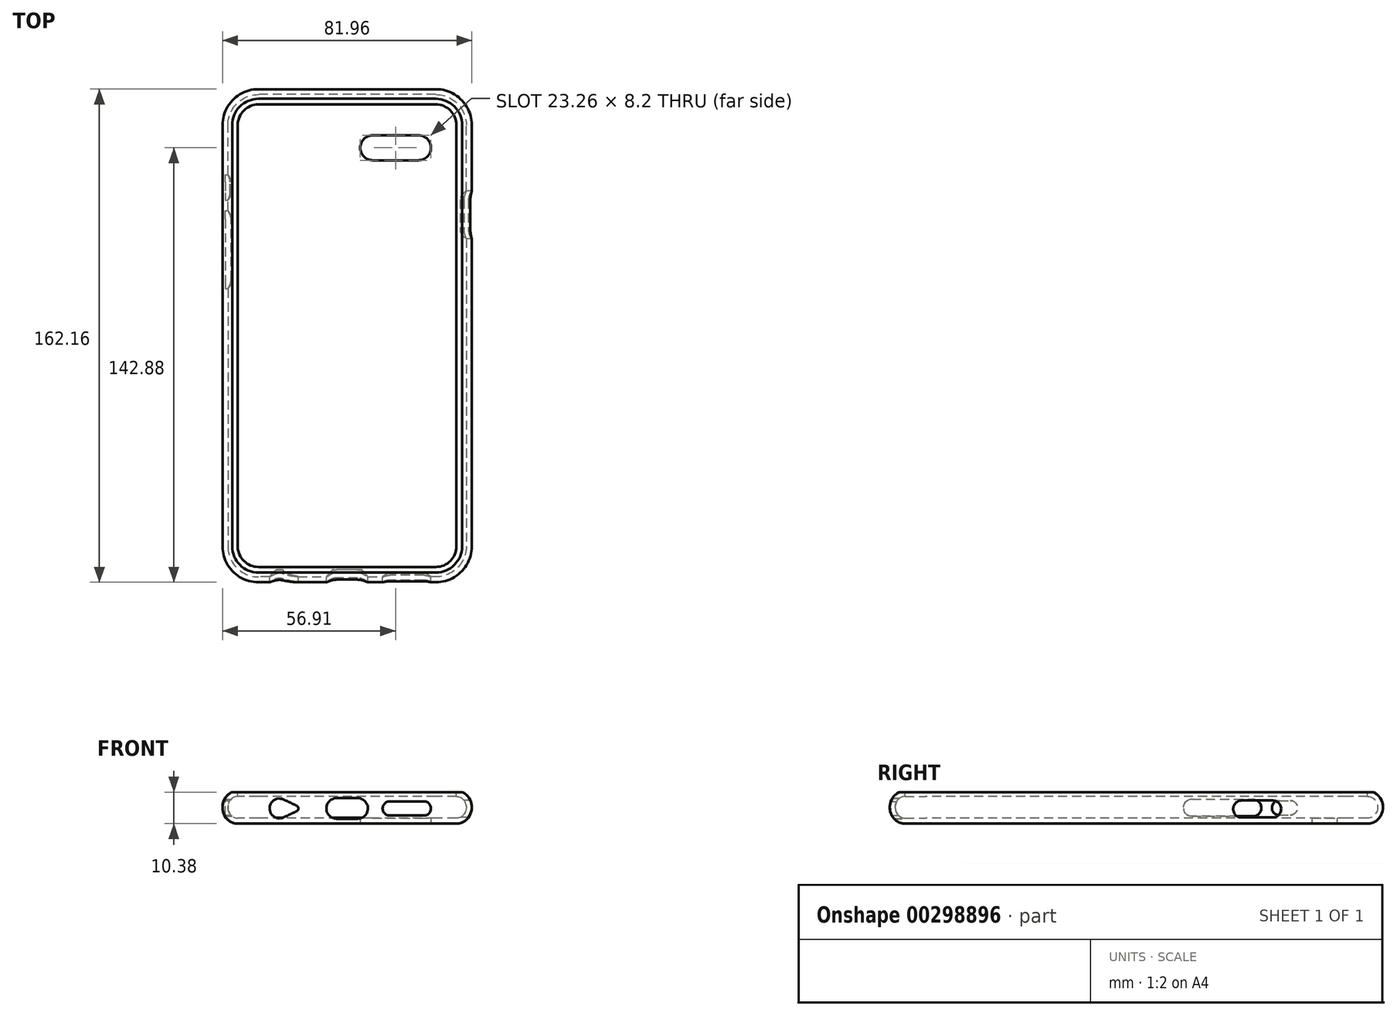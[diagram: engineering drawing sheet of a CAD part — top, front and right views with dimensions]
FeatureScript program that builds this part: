
annotation { "Feature Type Name" : "Feature", "Feature Type Description" : "" }
export const myFeature = defineFeature(function(context is Context, id is Id, definition is map)
    precondition{}
    {
        {
            var Q0;
            Q0=qCreatedBy(makeId("Top.planeOp"),FACE);
            var sketch = newSketch(context, id + "F0", { "sketchPlane" : qUnion([Q0])});
            skLineSegment(sketch, "E0.bottom", {"start": v(-41.5, 82.5) * mm, "end": v(41.5, 82.5) * mm});
            skLineSegment(sketch, "E0.top", {"start": v(-41.5, -82.5) * mm, "end": v(41.5, -82.5) * mm});
            skLineSegment(sketch, "E0.left", {"start": v(-41.5, 82.5) * mm, "end": v(-41.5, -82.5) * mm});
            skLineSegment(sketch, "E0.right", {"start": v(41.5, 82.5) * mm, "end": v(41.5, -82.5) * mm});
            skPoint(sketch, "E0.middle", {"position": v(0, 0) * mm});
            skSolve(sketch);
        }
        {
            var Q0;
            Q0=qSketchRegion(id+"F0",true);
            extrude(context, id + "F1", {"entities" : qUnion([Q0]), "depth" : 10 * mm});
        }
        {
            var Q0;
            Q0=makeQuery(id+"F1.opExtrude","CAP_FACE",FACE,{"disambiguationData":[OSD([sQuery(id+"F0.wireOp",EDGE,"E0.bottom"),sQuery(id+"F0.wireOp",EDGE,"E0.top"),sQuery(id+"F0.wireOp",EDGE,"E0.left"),sQuery(id+"F0.wireOp",EDGE,"E0.right")])],"isStart":false});
            var sketch = newSketch(context, id + "F2", { "sketchPlane" : qUnion([Q0])});
            skLineSegment(sketch, "E1.bottom", {"start": v(-29.15, 79.05) * mm, "end": v(29.15, 79.05) * mm});
            skLineSegment(sketch, "E1.top", {"start": v(-29.15, -79.05) * mm, "end": v(29.15, -79.05) * mm});
            skLineSegment(sketch, "E1.left", {"start": v(-38.95, 69.25) * mm, "end": v(-38.95, -69.25) * mm});
            skLineSegment(sketch, "E1.right", {"start": v(38.95, 69.25) * mm, "end": v(38.95, -69.25) * mm});
            skPoint(sketch, "E1.middle", {"position": v(0, 0) * mm});
            skPoint(sketch, "E2.visualSharp", {"position": v(-38.95, 79.05) * mm});
            skArc(sketch, "E2.filletArc", {"start": v(-29.15, 79.05) * mm, "mid": v(-36.08, 76.18) * mm, "end": v(-38.95, 69.25) * mm});
            skPoint(sketch, "E3.visualSharp", {"position": v(38.95, 79.05) * mm});
            skArc(sketch, "E3.filletArc", {"start": v(38.95, 69.25) * mm, "mid": v(36.08, 76.18) * mm, "end": v(29.15, 79.05) * mm});
            skPoint(sketch, "E4.visualSharp", {"position": v(38.95, -79.05) * mm});
            skArc(sketch, "E4.filletArc", {"start": v(29.15, -79.05) * mm, "mid": v(36.08, -76.18) * mm, "end": v(38.95, -69.25) * mm});
            skPoint(sketch, "E5.visualSharp", {"position": v(-38.95, -79.05) * mm});
            skArc(sketch, "E5.filletArc", {"start": v(-38.95, -69.25) * mm, "mid": v(-36.08, -76.18) * mm, "end": v(-29.15, -79.05) * mm});
            skSolve(sketch);
        }
        {
            var Q0;
            Q0=sQuery(id+"F2.wireOp",VERTEX,"E1.left.end");
            var Q1;
            Q1=sQuery(id+"F2.wireOp",EDGE,"E1.left");
            cPlane(context, id + "F3", {"entities" : qUnion([Q0, Q1]), "cplaneType" : CPlaneType.CURVE_POINT, "offset" : 25 * mm, "width" : 150 * mm, "height" : 150 * mm});
        }
        {
            var Q0;
            Q0=qCreatedBy(id+"F3.planeOp",FACE);
            var sketch = newSketch(context, id + "F4", { "sketchPlane" : qUnion([Q0])});
            skEllipse(sketch, "E6", {"center": v(-35.95, 5) * mm, "majorRadius": 3.6 * mm, "minorRadius": 3.25 * mm, "majorAxis": v(0, 1)});
            skLineSegment(sketch, "E7", {"start": v(0, 0) * mm, "end": v(0, 10) * mm});
            skPoint(sketch, "E8", {"position": v(-39.2, 5) * mm});
            skLineSegment(sketch, "E9", {"start": v(0, 5) * mm, "end": v(-39.2, 5) * mm});
            skPoint(sketch, "E10.oppositeSnap0", {"position": v(-35.95, 1.4) * mm});
            skPoint(sketch, "E11", {"position": v(-30.3, 10) * mm});
            skPoint(sketch, "E12", {"position": v(-32.78, 10) * mm});
            skPoint(sketch, "E13", {"position": v(-32.78, 1.4) * mm});
            skLineSegment(sketch, "E14.bottom", {"start": v(-35.95, 1.4) * mm, "end": v(-32.78, 1.4) * mm});
            skLineSegment(sketch, "E14.top", {"start": v(-35.95, 10) * mm, "end": v(-32.78, 10) * mm});
            skLineSegment(sketch, "E14.left", {"start": v(-35.95, 1.4) * mm, "end": v(-35.95, 10) * mm});
            skLineSegment(sketch, "E14.right", {"start": v(-32.78, 1.4) * mm, "end": v(-32.78, 10) * mm});
            skSolve(sketch);
        }
        {
            var Q0;
            Q0=qSketchRegion(id+"F4",true);
            var Q1;
            Q1=qConstructionFilter(qBodyType(qCreatedBy(id+"F2",EDGE),BodyType.WIRE),ConstructionObject.NO);
            sweep(context, id + "F5", {"operationType" : NewBodyOperationType.REMOVE, "profiles" : qUnion([Q0]), "path" : qUnion([Q1])});
        }
        {
            var Q0;
            {var subQ0=sQuery(id+"F4.wireOp",EDGE,"E14.right");var subQ1=makeQuery(id+"F4.imprint","IMPRINT",EDGE,{"disambiguationData":[TD([[makeQuery(id+"F4.imprint","INTERSECT",VERTEX,{"derivedFrom":[sQuery(id+"F4.wireOp",EDGE,"E14.top"),subQ0]}),1.0]])],"derivedFrom":subQ0});var subQ6=sQuery(id+"F2.wireOp",EDGE,"E1.bottom");Q0=makeQuery(id+"F5.boolean.opBoolean","SPLIT",FACE,{"disambiguationData":[TD([makeQuery(id+"F5.opSweep","SWEPT_FACE",FACE,{"disambiguationData":[OSD([subQ6,subQ0]),TDD([subQ6,subQ1])]})])],"derivedFrom":makeQuery(id+"F1.opExtrude","CAP_FACE",FACE,{"disambiguationData":[OSD([sQuery(id+"F0.wireOp",EDGE,"E0.bottom"),sQuery(id+"F0.wireOp",EDGE,"E0.top"),sQuery(id+"F0.wireOp",EDGE,"E0.left"),sQuery(id+"F0.wireOp",EDGE,"E0.right")])],"isStart":false})});}
            extrude(context, id + "F6", {"entities" : qUnion([Q0]), "operationType" : NewBodyOperationType.REMOVE, "oppositeDirection" : true, "depth" : 8.6 * mm});
        }
        {
            var Q0;
            Q0=makeQuery(id+"F1.opExtrude","CAP_FACE",FACE,{"disambiguationData":[OSD([sQuery(id+"F0.wireOp",EDGE,"E0.bottom"),sQuery(id+"F0.wireOp",EDGE,"E0.top"),sQuery(id+"F0.wireOp",EDGE,"E0.left"),sQuery(id+"F0.wireOp",EDGE,"E0.right")])],"isStart":true});
            var Q1;
            {var subQ1=sQuery(id+"F0.wireOp",EDGE,"E0.left");var subQ2=sQuery(id+"F0.wireOp",EDGE,"E0.bottom");var subQ3=sQuery(id+"F0.wireOp",EDGE,"E0.right");var subQ4=sQuery(id+"F0.wireOp",EDGE,"E0.top");Q1=makeQuery(id+"F5.boolean.opBoolean","SPLIT",FACE,{"disambiguationData":[TD([makeQuery(id+"F1.opExtrude","SWEPT_FACE",FACE,{"disambiguationData":[OSD([subQ2])]})])],"derivedFrom":makeQuery(id+"F1.opExtrude","CAP_FACE",FACE,{"disambiguationData":[OSD([subQ2,subQ4,subQ1,subQ3])],"isStart":false})});}
            var Q2;
            Q2=makeQuery(id+"F1.opExtrude","SWEPT_FACE",FACE,{"disambiguationData":[OSD([sQuery(id+"F0.wireOp",EDGE,"E0.top")])]});
            var Q3;
            Q3=makeQuery(id+"F1.opExtrude","SWEPT_FACE",FACE,{"disambiguationData":[OSD([sQuery(id+"F0.wireOp",EDGE,"E0.left")])]});
            var Q4;
            Q4=makeQuery(id+"F1.opExtrude","SWEPT_FACE",FACE,{"disambiguationData":[OSD([sQuery(id+"F0.wireOp",EDGE,"E0.bottom")])]});
            var Q5;
            Q5=makeQuery(id+"F1.opExtrude","SWEPT_FACE",FACE,{"disambiguationData":[OSD([sQuery(id+"F0.wireOp",EDGE,"E0.right")])]});
            shell(context, id + "F7", {"entities" : qUnion([Q0, Q1, Q2, Q3, Q4, Q5]), "thickness" : 1.78 * mm});
        }
        {
            var Q0;
            Q0=qCreatedBy(makeId("Front.planeOp"),FACE);
            var sketch = newSketch(context, id + "F8", { "sketchPlane" : qUnion([Q0])});
            skLineSegment(sketch, "E15.rect.bottom", {"start": v(3.43, 1.22) * mm, "end": v(-3.42, 1.22) * mm});
            skLineSegment(sketch, "E15.rect.top", {"start": v(3.42, 8.02) * mm, "end": v(-3.43, 8.02) * mm});
            skLineSegment(sketch, "E15.rect.left", {"start": v(3.43, 1.22) * mm, "end": v(3.42, 8.02) * mm, "construction": true});
            skLineSegment(sketch, "E15.rect.right", {"start": v(-3.43, 1.22) * mm, "end": v(-3.43, 8.02) * mm, "construction": true});
            skPoint(sketch, "E15.rect.middle", {"position": v(0, 4.62) * mm});
            skArc(sketch, "E16", {"start": v(-3.42, 8.02) * mm, "mid": v(-6.83, 4.62) * mm, "end": v(-3.43, 1.22) * mm});
            skArc(sketch, "E17", {"start": v(3.43, 1.22) * mm, "mid": v(6.82, 4.62) * mm, "end": v(3.42, 8.02) * mm});
            skArc(sketch, "E18", {"start": v(-20.85, 7.55) * mm, "mid": v(-25.5, 4.62) * mm, "end": v(-20.85, 1.69) * mm});
            skLineSegment(sketch, "E19", {"start": v(3.42, 4.62) * mm, "end": v(19.62, 4.62) * mm, "construction": true});
            skLineSegment(sketch, "E20.rect.bottom", {"start": v(25.24, 3.82) * mm, "end": v(14, 3.82) * mm, "construction": true});
            skLineSegment(sketch, "E20.rect.top", {"start": v(25.24, 5.42) * mm, "end": v(14, 5.42) * mm, "construction": true});
            skLineSegment(sketch, "E20.rect.left", {"start": v(25.24, 3.82) * mm, "end": v(25.24, 5.42) * mm, "construction": true});
            skLineSegment(sketch, "E20.rect.right", {"start": v(14, 3.82) * mm, "end": v(14, 5.42) * mm, "construction": true});
            skPoint(sketch, "E20.rect.middle", {"position": v(19.62, 4.62) * mm});
            skArc(sketch, "E21", {"start": v(14, 5.42) * mm, "mid": v(13.2, 4.62) * mm, "end": v(14, 3.82) * mm, "construction": true});
            skArc(sketch, "E22", {"start": v(25.24, 3.82) * mm, "mid": v(26.04, 4.62) * mm, "end": v(25.24, 5.42) * mm, "construction": true});
            skArc(sketch, "E23.0", {"start": v(14, 6.95) * mm, "mid": v(11.67, 4.62) * mm, "end": v(14, 2.3) * mm});
            skLineSegment(sketch, "E23.1", {"start": v(25.24, 6.95) * mm, "end": v(14, 6.95) * mm});
            skArc(sketch, "E23.2", {"start": v(25.24, 2.3) * mm, "mid": v(27.57, 4.62) * mm, "end": v(25.24, 6.95) * mm});
            skLineSegment(sketch, "E23.3", {"start": v(25.24, 2.3) * mm, "end": v(14, 2.3) * mm});
            skArc(sketch, "E24", {"start": v(-16.6, 3.72) * mm, "mid": v(-16.03, 4.62) * mm, "end": v(-16.6, 5.52) * mm});
            skLineSegment(sketch, "E25", {"start": v(-20.85, 7.55) * mm, "end": v(-16.6, 5.52) * mm});
            skLineSegment(sketch, "E26", {"start": v(-20.85, 1.69) * mm, "end": v(-16.6, 3.72) * mm});
            skPoint(sketch, "E27", {"position": v(0, 1.22) * mm});
            skLineSegment(sketch, "E28", {"start": v(0, -0.38) * mm, "end": v(0, 4.62) * mm});
            skSolve(sketch);
        }
        {
            var Q0;
            Q0=qSketchRegion(id+"F8",true);
            extrude(context, id + "F9", {"entities" : qUnion([Q0]), "operationType" : NewBodyOperationType.REMOVE, "depth" : 90 * mm, "hasSecondDirection" : true, "secondDirectionOppositeDirection" : false, "secondDirectionDepth" : 77 * mm});
        }
        {
            var Q0;
            Q0=qCreatedBy(makeId("Top.planeOp"),FACE);
            var sketch = newSketch(context, id + "F10", { "sketchPlane" : qUnion([Q0])});
            skArc(sketch, "E29", {"start": v(23.46, 57.7) * mm, "mid": v(27.56, 61.8) * mm, "end": v(23.46, 65.9) * mm});
            skArc(sketch, "E30", {"start": v(8.4, 65.9) * mm, "mid": v(4.3, 61.8) * mm, "end": v(8.4, 57.7) * mm});
            skLineSegment(sketch, "E31", {"start": v(8.4, 65.9) * mm, "end": v(23.46, 65.9) * mm});
            skLineSegment(sketch, "E32", {"start": v(8.4, 57.7) * mm, "end": v(23.46, 57.7) * mm});
            skSolve(sketch);
        }
        {
            var Q0;
            Q0=qSketchRegion(id+"F10",true);
            extrude(context, id + "F11", {"entities" : qUnion([Q0]), "operationType" : NewBodyOperationType.REMOVE, "endBound" : BoundingType.SYMMETRIC, "depth" : 12.5 * mm});
        }
        {
            var Q0;
            Q0=qCreatedBy(makeId("Right.planeOp"),FACE);
            var sketch = newSketch(context, id + "F12", { "sketchPlane" : qUnion([Q0])});
            skLineSegment(sketch, "E33", {"start": v(5.28, 4.82) * mm, "end": v(44.55, 4.82) * mm, "construction": true});
            skLineSegment(sketch, "E34.rect.bottom", {"start": v(50.59, 5.81) * mm, "end": v(46.96, 5.81) * mm, "construction": true});
            skLineSegment(sketch, "E34.rect.top", {"start": v(50.59, 3.83) * mm, "end": v(46.96, 3.83) * mm, "construction": true});
            skLineSegment(sketch, "E34.rect.left", {"start": v(50.59, 5.81) * mm, "end": v(50.59, 3.83) * mm, "construction": true});
            skLineSegment(sketch, "E34.rect.right", {"start": v(46.96, 5.81) * mm, "end": v(46.96, 3.83) * mm, "construction": true});
            skPoint(sketch, "E34.rect.middle", {"position": v(48.77, 4.82) * mm});
            skLineSegment(sketch, "E35.rect.bottom", {"start": v(38.28, 6.22) * mm, "end": v(18.27, 6.22) * mm, "construction": true});
            skLineSegment(sketch, "E35.rect.top", {"start": v(38.28, 3.42) * mm, "end": v(18.27, 3.42) * mm, "construction": true});
            skLineSegment(sketch, "E35.rect.left", {"start": v(38.28, 6.22) * mm, "end": v(38.28, 3.42) * mm, "construction": true});
            skLineSegment(sketch, "E35.rect.right", {"start": v(18.27, 6.22) * mm, "end": v(18.27, 3.42) * mm, "construction": true});
            skPoint(sketch, "E35.rect.middle", {"position": v(28.27, 4.82) * mm});
            skArc(sketch, "E36", {"start": v(18.27, 6.22) * mm, "mid": v(16.87, 4.82) * mm, "end": v(18.27, 3.42) * mm, "construction": true});
            skArc(sketch, "E37", {"start": v(38.28, 3.42) * mm, "mid": v(39.68, 4.82) * mm, "end": v(38.28, 6.22) * mm, "construction": true});
            skArc(sketch, "E38", {"start": v(46.96, 5.81) * mm, "mid": v(45.97, 4.82) * mm, "end": v(46.96, 3.83) * mm, "construction": true});
            skArc(sketch, "E39", {"start": v(50.59, 3.83) * mm, "mid": v(51.58, 4.82) * mm, "end": v(50.59, 5.81) * mm, "construction": true});
            skLineSegment(sketch, "E40.0", {"start": v(38.28, 7.62) * mm, "end": v(18.27, 7.62) * mm});
            skArc(sketch, "E40.1", {"start": v(38.28, 2.02) * mm, "mid": v(41.08, 4.82) * mm, "end": v(38.28, 7.62) * mm});
            skLineSegment(sketch, "E40.2", {"start": v(38.28, 2.02) * mm, "end": v(18.27, 2.02) * mm});
            skArc(sketch, "E40.3", {"start": v(18.27, 7.62) * mm, "mid": v(15.47, 4.82) * mm, "end": v(18.27, 2.02) * mm});
            skLineSegment(sketch, "E41.0", {"start": v(50.59, 7.2) * mm, "end": v(46.96, 7.2) * mm});
            skArc(sketch, "E41.1", {"start": v(50.59, 2.43) * mm, "mid": v(52.98, 4.82) * mm, "end": v(50.59, 7.2) * mm});
            skLineSegment(sketch, "E41.2", {"start": v(50.59, 2.43) * mm, "end": v(46.96, 2.43) * mm});
            skArc(sketch, "E41.3", {"start": v(46.96, 7.2) * mm, "mid": v(44.57, 4.82) * mm, "end": v(46.96, 2.43) * mm});
            skSolve(sketch);
        }
        {
            var Q0;
            Q0=qSketchRegion(id+"F12",true);
            extrude(context, id + "F13", {"entities" : qUnion([Q0]), "operationType" : NewBodyOperationType.REMOVE, "oppositeDirection" : true, "depth" : 40 * mm});
        }
        {
            var Q0;
            Q0=qCreatedBy(makeId("Right.planeOp"),FACE);
            var sketch = newSketch(context, id + "F14", { "sketchPlane" : qUnion([Q0])});
            skLineSegment(sketch, "E42", {"start": v(34.62, 4.44) * mm, "end": v(44.82, 4.44) * mm, "construction": true});
            skArc(sketch, "E43.0.startCap", {"start": v(34.62, 1.65) * mm, "mid": v(31.83, 4.44) * mm, "end": v(34.62, 7.24) * mm});
            skArc(sketch, "E43.0.endCap", {"start": v(44.82, 7.24) * mm, "mid": v(47.61, 4.44) * mm, "end": v(44.82, 1.65) * mm});
            skLineSegment(sketch, "E43.0.left", {"start": v(34.62, 7.24) * mm, "end": v(44.82, 7.24) * mm});
            skLineSegment(sketch, "E43.0.right", {"start": v(34.62, 1.65) * mm, "end": v(44.82, 1.65) * mm});
            skPoint(sketch, "E44", {"position": v(39.72, 4.44) * mm});
            skSolve(sketch);
        }
        {
            var Q0;
            Q0=qSketchRegion(id+"F14",true);
            extrude(context, id + "F15", {"entities" : qUnion([Q0]), "operationType" : NewBodyOperationType.REMOVE, "depth" : 45 * mm});
        }
    });
